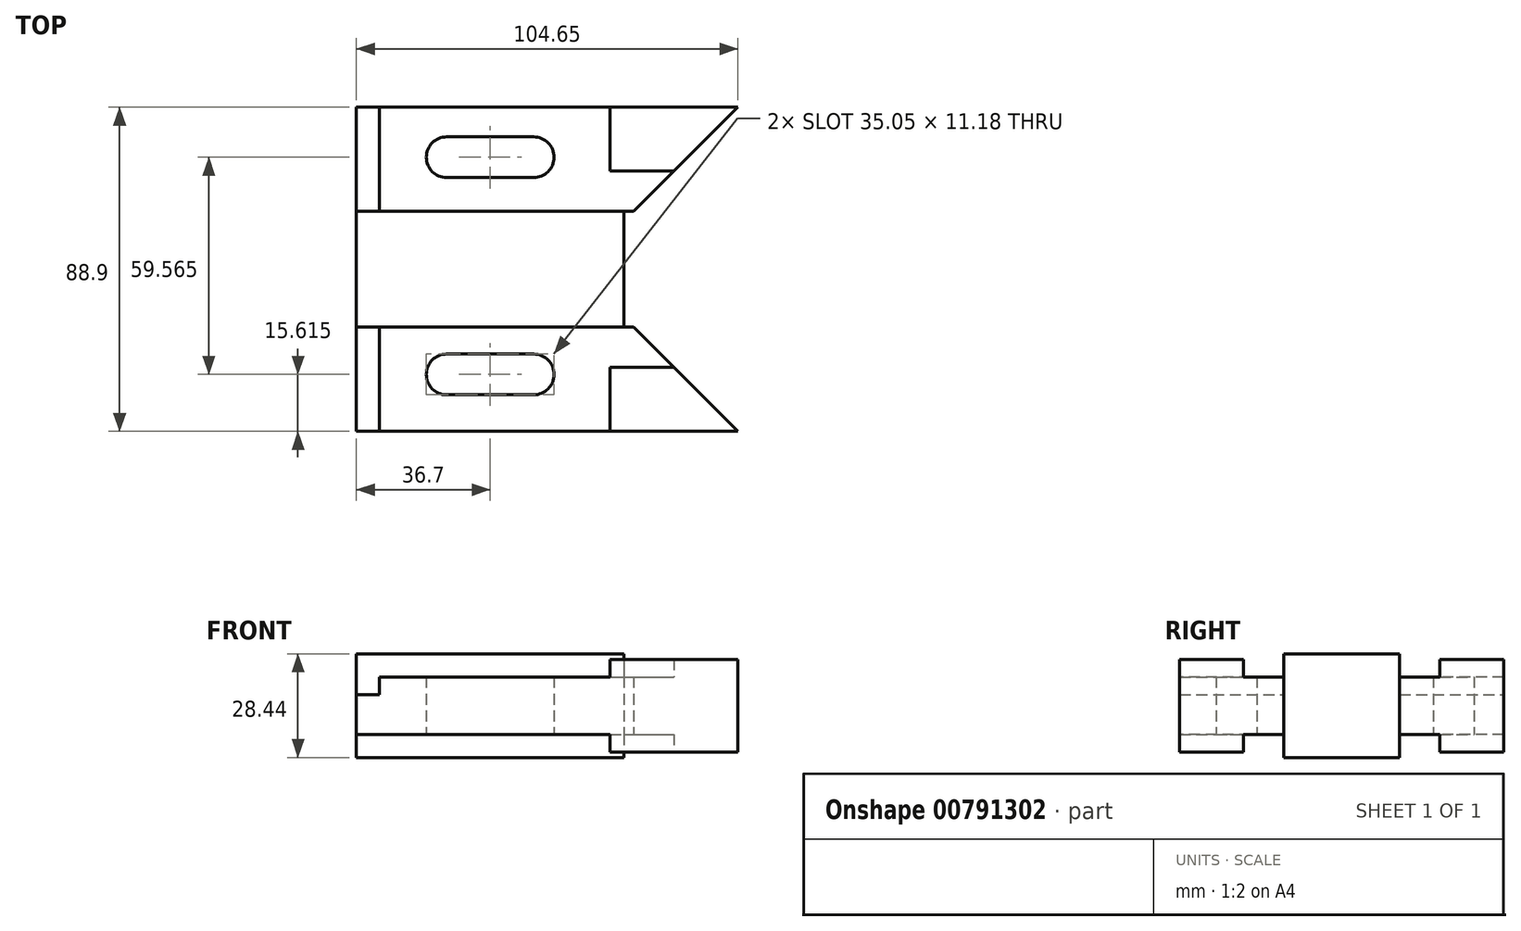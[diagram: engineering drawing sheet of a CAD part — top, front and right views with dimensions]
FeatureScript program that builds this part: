
annotation { "Feature Type Name" : "Feature", "Feature Type Description" : "" }
export const myFeature = defineFeature(function(context is Context, id is Id, definition is map)
    precondition{}
    {
        {
            var Q0;
            Q0=qCreatedBy(makeId("Top.planeOp"),FACE);
            var sketch = newSketch(context, id + "F0", { "sketchPlane" : qUnion([Q0])});
            skLineSegment(sketch, "E0.bottom", {"start": v(36.7, -44.45) * mm, "end": v(-36.7, -44.45) * mm});
            skLineSegment(sketch, "E0.top", {"start": v(36.7, 44.45) * mm, "end": v(-36.7, 44.45) * mm});
            skLineSegment(sketch, "E0.left", {"start": v(36.7, -44.45) * mm, "end": v(36.7, 44.45) * mm});
            skLineSegment(sketch, "E0.right", {"start": v(-36.7, -44.45) * mm, "end": v(-36.7, 44.45) * mm});
            skPoint(sketch, "E0.middle", {"position": v(0, 0) * mm});
            skLineSegment(sketch, "E1", {"start": v(-36.7, 15.87) * mm, "end": v(36.7, 15.88) * mm});
            skLineSegment(sketch, "E2", {"start": v(-36.7, -15.88) * mm, "end": v(36.7, -15.87) * mm});
            skLineSegment(sketch, "E3", {"start": v(-30.35, 44.45) * mm, "end": v(-30.35, 15.88) * mm});
            skLineSegment(sketch, "E4", {"start": v(-30.35, -15.87) * mm, "end": v(-30.35, -44.45) * mm});
            skLineSegment(sketch, "E5.bottom", {"start": v(11.94, 25.14) * mm, "end": v(-11.94, 25.14) * mm});
            skLineSegment(sketch, "E5.top", {"start": v(11.94, 36.32) * mm, "end": v(-11.94, 36.32) * mm});
            skLineSegment(sketch, "E5.left", {"start": v(17.53, 30.73) * mm, "end": v(17.53, 30.73) * mm});
            skLineSegment(sketch, "E5.right", {"start": v(-17.53, 30.73) * mm, "end": v(-17.53, 30.73) * mm});
            skPoint(sketch, "E5.middle", {"position": v(0, 30.73) * mm});
            skLineSegment(sketch, "E6.bottom", {"start": v(11.94, -34.42) * mm, "end": v(-11.94, -34.42) * mm});
            skLineSegment(sketch, "E6.top", {"start": v(11.94, -23.25) * mm, "end": v(-11.94, -23.25) * mm});
            skLineSegment(sketch, "E6.left", {"start": v(17.53, -28.84) * mm, "end": v(17.53, -28.84) * mm});
            skLineSegment(sketch, "E6.right", {"start": v(-17.53, -28.84) * mm, "end": v(-17.53, -28.84) * mm});
            skPoint(sketch, "E6.middle", {"position": v(0, -28.84) * mm});
            skPoint(sketch, "E7.visualSharp", {"position": v(17.53, -23.25) * mm});
            skArc(sketch, "E7.filletArc", {"start": v(17.53, -28.84) * mm, "mid": v(15.89, -24.88) * mm, "end": v(11.94, -23.25) * mm});
            skPoint(sketch, "E8.visualSharp", {"position": v(-17.53, -34.42) * mm});
            skArc(sketch, "E8.filletArc", {"start": v(-17.53, -28.84) * mm, "mid": v(-15.89, -32.79) * mm, "end": v(-11.94, -34.42) * mm});
            skPoint(sketch, "E9.visualSharp", {"position": v(17.53, -34.42) * mm});
            skArc(sketch, "E9.filletArc", {"start": v(11.94, -34.42) * mm, "mid": v(15.89, -32.79) * mm, "end": v(17.53, -28.84) * mm});
            skPoint(sketch, "E10.visualSharp", {"position": v(-17.53, -23.25) * mm});
            skArc(sketch, "E10.filletArc", {"start": v(-11.94, -23.25) * mm, "mid": v(-15.89, -24.88) * mm, "end": v(-17.53, -28.84) * mm});
            skPoint(sketch, "E11.visualSharp", {"position": v(-17.53, 25.14) * mm});
            skArc(sketch, "E11.filletArc", {"start": v(-17.53, 30.73) * mm, "mid": v(-15.89, 26.78) * mm, "end": v(-11.94, 25.14) * mm});
            skPoint(sketch, "E12.visualSharp", {"position": v(17.53, 25.14) * mm});
            skArc(sketch, "E12.filletArc", {"start": v(11.94, 25.14) * mm, "mid": v(15.89, 26.78) * mm, "end": v(17.53, 30.73) * mm});
            skPoint(sketch, "E13.visualSharp", {"position": v(17.53, 36.32) * mm});
            skArc(sketch, "E13.filletArc", {"start": v(17.53, 30.73) * mm, "mid": v(15.89, 34.68) * mm, "end": v(11.94, 36.32) * mm});
            skPoint(sketch, "E14.visualSharp", {"position": v(-17.53, 36.32) * mm});
            skArc(sketch, "E14.filletArc", {"start": v(-11.94, 36.32) * mm, "mid": v(-15.89, 34.68) * mm, "end": v(-17.53, 30.73) * mm});
            skLineSegment(sketch, "E15", {"start": v(36.7, 15.88) * mm, "end": v(39.37, 15.88) * mm});
            skLineSegment(sketch, "E16", {"start": v(39.37, 15.88) * mm, "end": v(67.94, 44.45) * mm});
            skLineSegment(sketch, "E17", {"start": v(67.94, 44.45) * mm, "end": v(36.7, 44.45) * mm});
            skLineSegment(sketch, "E18", {"start": v(36.7, -15.87) * mm, "end": v(39.37, -15.87) * mm});
            skLineSegment(sketch, "E19", {"start": v(39.37, -15.87) * mm, "end": v(67.95, -44.45) * mm});
            skLineSegment(sketch, "E20", {"start": v(67.95, -44.45) * mm, "end": v(36.7, -44.45) * mm});
            skLineSegment(sketch, "E21", {"start": v(32.9, 44.45) * mm, "end": v(32.9, 26.92) * mm});
            skLineSegment(sketch, "E22", {"start": v(32.9, 26.92) * mm, "end": v(50.42, 26.92) * mm});
            skLineSegment(sketch, "E23", {"start": v(32.9, -44.45) * mm, "end": v(32.9, -26.92) * mm});
            skLineSegment(sketch, "E24", {"start": v(32.9, -26.92) * mm, "end": v(50.42, -26.92) * mm});
            skSolve(sketch);
        }
        {
            var Q0;
            {var subQ0=sQuery(id+"F0.wireOp",EDGE,"E1");var subQ1=sQuery(id+"F0.wireOp",EDGE,"E0.left");var subQ2=makeQuery(id+"F0.imprint","INTERSECT",VERTEX,{"derivedFrom":[subQ1,subQ0]});Q0=makeQuery(id+"F0.imprint","IMPRINT",FACE,{"disambiguationData":[TD([[makeQuery(id+"F0.imprint","IMPRINT",EDGE,{"disambiguationData":[TD([[subQ2,1.0]])],"derivedFrom":subQ1}),1.0]])]});}
            extrude(context, id + "F1", {"entities" : qUnion([Q0]), "endBound" : BoundingType.SYMMETRIC, "depth" : 28.45 * mm, "offsetDistance" : 25.4 * mm});
        }
        {
            var Q0;
            {var subQ0=sQuery(id+"F0.wireOp",EDGE,"E3");Q0=makeQuery(id+"F0.imprint","IMPRINT",FACE,{"disambiguationData":[TD([[makeQuery(id+"F0.imprint","IMPRINT",EDGE,{"derivedFrom":subQ0}),1.0]])]});}
            var Q1;
            {var subQ3=sQuery(id+"F0.wireOp",EDGE,"E4");Q1=makeQuery(id+"F0.imprint","IMPRINT",FACE,{"disambiguationData":[TD([[makeQuery(id+"F0.imprint","IMPRINT",EDGE,{"derivedFrom":subQ3}),1.0]])]});}
            var Q2;
            {var subQ0=sQuery(id+"F0.wireOp",EDGE,"E15");Q2=makeQuery(id+"F0.imprint","IMPRINT",FACE,{"disambiguationData":[TD([[makeQuery(id+"F0.imprint","IMPRINT",EDGE,{"derivedFrom":subQ0}),1.0]])]});}
            var Q3;
            {var subQ0=sQuery(id+"F0.wireOp",EDGE,"E18");Q3=makeQuery(id+"F0.imprint","IMPRINT",FACE,{"disambiguationData":[TD([[makeQuery(id+"F0.imprint","IMPRINT",EDGE,{"derivedFrom":subQ0}),-1.0]])]});}
            extrude(context, id + "F2", {"entities" : qUnion([Q0, Q1, Q2, Q3]), "operationType" : NewBodyOperationType.ADD, "endBound" : BoundingType.SYMMETRIC, "depth" : 15.75 * mm, "offsetDistance" : 25.4 * mm});
        }
        {
            var Q0;
            {var subQ3=sQuery(id+"F0.wireOp",EDGE,"E3");Q0=makeQuery(id+"F0.imprint","IMPRINT",FACE,{"disambiguationData":[TD([[makeQuery(id+"F0.imprint","IMPRINT",EDGE,{"derivedFrom":subQ3}),-1.0]])]});}
            var Q1;
            {var subQ3=sQuery(id+"F0.wireOp",EDGE,"E4");Q1=makeQuery(id+"F0.imprint","IMPRINT",FACE,{"disambiguationData":[TD([[makeQuery(id+"F0.imprint","IMPRINT",EDGE,{"derivedFrom":subQ3}),-1.0]])]});}
            extrude(context, id + "F3", {"entities" : qUnion([Q0, Q1]), "operationType" : NewBodyOperationType.ADD, "depth" : 3.05 * mm, "offsetDistance" : 25.4 * mm});
        }
        {
            var Q0;
            {var subQ3=sQuery(id+"F0.wireOp",EDGE,"E4");Q0=makeQuery(id+"F0.imprint","IMPRINT",FACE,{"disambiguationData":[TD([[makeQuery(id+"F0.imprint","IMPRINT",EDGE,{"derivedFrom":subQ3}),-1.0]])]});}
            var Q1;
            {var subQ3=sQuery(id+"F0.wireOp",EDGE,"E3");Q1=makeQuery(id+"F0.imprint","IMPRINT",FACE,{"disambiguationData":[TD([[makeQuery(id+"F0.imprint","IMPRINT",EDGE,{"derivedFrom":subQ3}),-1.0]])]});}
            var Q2;
            Q2=makeQuery(id+"F2.opExtrude","CAP_FACE",FACE,{"disambiguationData":[OSD([sQuery(id+"F0.wireOp",EDGE,"E0.bottom"),sQuery(id+"F0.wireOp",EDGE,"E0.left"),sQuery(id+"F0.wireOp",EDGE,"E2"),sQuery(id+"F0.wireOp",EDGE,"E4"),sQuery(id+"F0.wireOp",EDGE,"E6.bottom"),sQuery(id+"F0.wireOp",EDGE,"E6.top"),sQuery(id+"F0.wireOp",EDGE,"E7.filletArc"),sQuery(id+"F0.wireOp",EDGE,"E8.filletArc"),sQuery(id+"F0.wireOp",EDGE,"E9.filletArc"),sQuery(id+"F0.wireOp",EDGE,"E10.filletArc")])],"isStart":true});
            extrude(context, id + "F4", {"entities" : qUnion([Q0, Q1]), "operationType" : NewBodyOperationType.ADD, "endBound" : BoundingType.UP_TO_SURFACE, "oppositeDirection" : true, "depth" : 25.4 * mm, "endBoundEntityFace" : qUnion([Q2]), "offsetDistance" : 25.4 * mm});
        }
        {
            var Q0;
            {var subQ0=sQuery(id+"F0.wireOp",EDGE,"E20");Q0=makeQuery(id+"F0.imprint","IMPRINT",FACE,{"disambiguationData":[TD([[makeQuery(id+"F0.imprint","IMPRINT",EDGE,{"derivedFrom":subQ0}),-1.0]])]});}
            var Q1;
            {var subQ3=sQuery(id+"F0.wireOp",EDGE,"E23");Q1=makeQuery(id+"F0.imprint","IMPRINT",FACE,{"disambiguationData":[TD([[makeQuery(id+"F0.imprint","IMPRINT",EDGE,{"derivedFrom":subQ3}),-1.0]])]});}
            var Q2;
            {var subQ0=sQuery(id+"F0.wireOp",EDGE,"E17");Q2=makeQuery(id+"F0.imprint","IMPRINT",FACE,{"disambiguationData":[TD([[makeQuery(id+"F0.imprint","IMPRINT",EDGE,{"derivedFrom":subQ0}),1.0]])]});}
            var Q3;
            {var subQ3=sQuery(id+"F0.wireOp",EDGE,"E21");Q3=makeQuery(id+"F0.imprint","IMPRINT",FACE,{"disambiguationData":[TD([[makeQuery(id+"F0.imprint","IMPRINT",EDGE,{"derivedFrom":subQ3}),1.0]])]});}
            extrude(context, id + "F5", {"entities" : qUnion([Q0, Q1, Q2, Q3]), "operationType" : NewBodyOperationType.ADD, "endBound" : BoundingType.SYMMETRIC, "depth" : 25.4 * mm, "offsetDistance" : 25.4 * mm});
        }
    });
